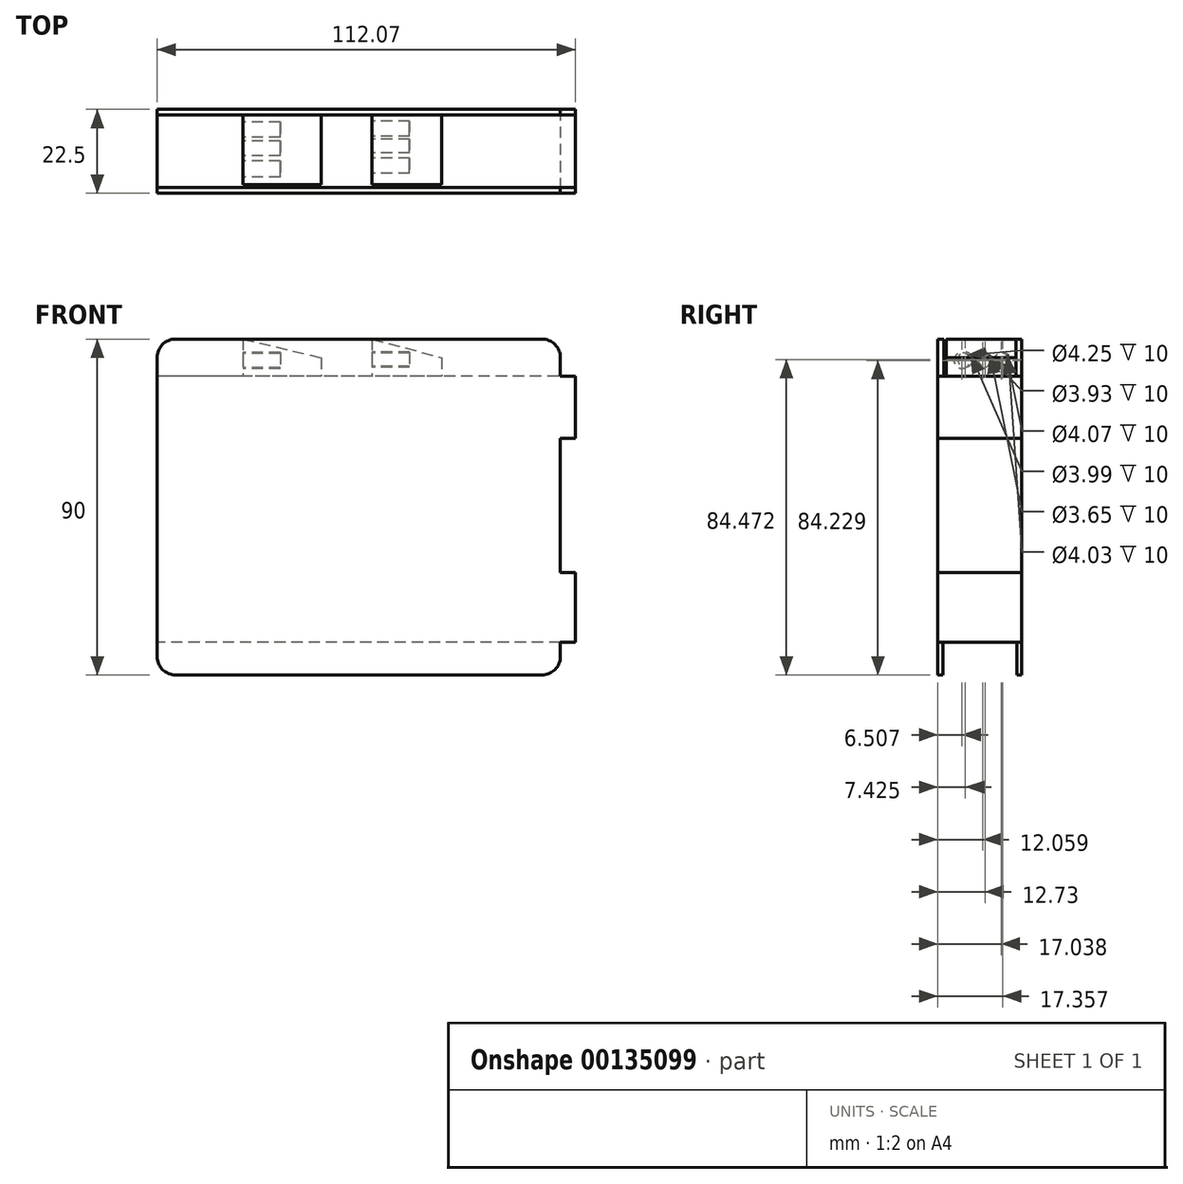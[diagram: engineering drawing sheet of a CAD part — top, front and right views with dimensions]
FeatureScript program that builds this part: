
annotation { "Feature Type Name" : "Feature", "Feature Type Description" : "" }
export const myFeature = defineFeature(function(context is Context, id is Id, definition is map)
    precondition{}
    {
        {
            var Q0;
            Q0=qCreatedBy(makeId("Front.planeOp"),FACE);
            var sketch = newSketch(context, id + "F0", { "sketchPlane" : qUnion([Q0])});
            skLineSegment(sketch, "E0.bottom", {"start": v(-39, -35.05) * mm, "end": v(59, -35.05) * mm});
            skLineSegment(sketch, "E0.top", {"start": v(-39, 54.95) * mm, "end": v(59, 54.95) * mm});
            skLineSegment(sketch, "E0.left", {"start": v(-44, -30.05) * mm, "end": v(-44, 49.95) * mm});
            skLineSegment(sketch, "E0.right", {"start": v(64, -30.05) * mm, "end": v(64, 49.95) * mm});
            skPoint(sketch, "E1.visualSharp", {"position": v(-44, 54.95) * mm});
            skArc(sketch, "E1.filletArc", {"start": v(-39, 54.95) * mm, "mid": v(-42.53, 53.49) * mm, "end": v(-44, 49.95) * mm});
            skPoint(sketch, "E2.visualSharp", {"position": v(64, 54.95) * mm});
            skArc(sketch, "E2.filletArc", {"start": v(64, 49.95) * mm, "mid": v(62.54, 53.49) * mm, "end": v(59, 54.95) * mm});
            skPoint(sketch, "E3.visualSharp", {"position": v(64, -35.05) * mm});
            skArc(sketch, "E3.filletArc", {"start": v(59, -35.05) * mm, "mid": v(62.54, -33.58) * mm, "end": v(64, -30.05) * mm});
            skPoint(sketch, "E4.visualSharp", {"position": v(-44, -35.05) * mm});
            skArc(sketch, "E4.filletArc", {"start": v(-44, -30.05) * mm, "mid": v(-42.53, -33.58) * mm, "end": v(-39, -35.05) * mm});
            skSolve(sketch);
        }
        {
            var Q0;
            Q0=makeQuery(id+"F0.imprint","IMPRINT",FACE,{"disambiguationData":[TD([[makeQuery(id+"F0.imprint","IMPRINT",EDGE,{"derivedFrom":sQuery(id+"F0.wireOp",EDGE,"E0.bottom")}),1.0]])]});
            extrude(context, id + "F1", {"entities" : qUnion([Q0]), "depth" : 22.5 * mm});
        }
        {
            var Q0;
            Q0=makeQuery(id+"F1.opExtrude","SWEPT_FACE",FACE,{"disambiguationData":[OSD([sQuery(id+"F0.wireOp",EDGE,"E0.left")])]});
            var sketch = newSketch(context, id + "F2", { "sketchPlane" : qUnion([Q0])});
            skLineSegment(sketch, "E5.bottom", {"start": v(1.51, 56.28) * mm, "end": v(20.87, 56.28) * mm});
            skLineSegment(sketch, "E5.top", {"start": v(1.51, 44.94) * mm, "end": v(20.87, 44.94) * mm});
            skLineSegment(sketch, "E5.left", {"start": v(1.51, 56.28) * mm, "end": v(1.51, 44.94) * mm});
            skLineSegment(sketch, "E5.right", {"start": v(20.87, 56.28) * mm, "end": v(20.87, 44.94) * mm});
            skLineSegment(sketch, "E6.bottom", {"start": v(1.34, -36.68) * mm, "end": v(21.04, -36.68) * mm});
            skLineSegment(sketch, "E6.top", {"start": v(1.34, -26.21) * mm, "end": v(21.04, -26.21) * mm});
            skLineSegment(sketch, "E6.left", {"start": v(1.34, -36.68) * mm, "end": v(1.34, -26.21) * mm});
            skLineSegment(sketch, "E6.right", {"start": v(21.04, -36.68) * mm, "end": v(21.04, -26.21) * mm});
            skSolve(sketch);
        }
        {
            var Q0;
            {var subQ0=sQuery(id+"F2.wireOp",EDGE,"E5.bottom");Q0=makeQuery(id+"F2.imprint","IMPRINT",FACE,{"disambiguationData":[TD([[makeQuery(id+"F2.imprint","IMPRINT",EDGE,{"derivedFrom":subQ0}),-1.0]])]});}
            var Q1;
            {var subQ0=sQuery(id+"F2.wireOp",EDGE,"E5.top");Q1=makeQuery(id+"F2.imprint","IMPRINT",FACE,{"disambiguationData":[TD([[makeQuery(id+"F2.imprint","IMPRINT",EDGE,{"derivedFrom":subQ0}),1.0]])]});}
            var Q2;
            {var subQ0=sQuery(id+"F2.wireOp",EDGE,"E6.top");Q2=makeQuery(id+"F2.imprint","IMPRINT",FACE,{"disambiguationData":[TD([[makeQuery(id+"F2.imprint","IMPRINT",EDGE,{"derivedFrom":subQ0}),-1.0]])]});}
            var Q3;
            {var subQ0=sQuery(id+"F2.wireOp",EDGE,"E6.bottom");Q3=makeQuery(id+"F2.imprint","IMPRINT",FACE,{"disambiguationData":[TD([[makeQuery(id+"F2.imprint","IMPRINT",EDGE,{"derivedFrom":subQ0}),1.0]])]});}
            extrude(context, id + "F3", {"entities" : qUnion([Q0, Q1, Q2, Q3]), "operationType" : NewBodyOperationType.REMOVE, "oppositeDirection" : true, "depth" : 155.21 * mm});
        }
        {
            var Q0;
            Q0=makeQuery(id+"F3.boolean.opBoolean","COPY",FACE,{"derivedFrom":makeQuery(id+"F3.opExtrude","SWEPT_FACE",FACE,{"disambiguationData":[OSD([sQuery(id+"F2.wireOp",EDGE,"E5.left")])]})});
            var sketch = newSketch(context, id + "F4", { "sketchPlane" : qUnion([Q0])});
            skLineSegment(sketch, "E7.bottom", {"start": v(-21.03, 54.95) * mm, "end": v(0, 54.95) * mm});
            skLineSegment(sketch, "E7.top", {"start": v(-21.03, 44.94) * mm, "end": v(0, 44.94) * mm});
            skLineSegment(sketch, "E7.left", {"start": v(-21.03, 54.95) * mm, "end": v(-21.03, 44.94) * mm});
            skLineSegment(sketch, "E7.right", {"start": v(0, 54.95) * mm, "end": v(0, 44.94) * mm});
            skLineSegment(sketch, "E8.bottom", {"start": v(13.6, 54.95) * mm, "end": v(32.2, 54.95) * mm});
            skLineSegment(sketch, "E8.top", {"start": v(13.6, 44.94) * mm, "end": v(32.2, 44.94) * mm});
            skLineSegment(sketch, "E8.left", {"start": v(13.6, 54.95) * mm, "end": v(13.6, 44.94) * mm});
            skLineSegment(sketch, "E8.right", {"start": v(32.2, 54.95) * mm, "end": v(32.2, 44.94) * mm});
            skLineSegment(sketch, "E9", {"start": v(-21.03, 54.95) * mm, "end": v(0, 49.95) * mm});
            skLineSegment(sketch, "E10", {"start": v(13.6, 54.95) * mm, "end": v(32.2, 49.95) * mm});
            skSolve(sketch);
        }
        {
            var Q0;
            {var subQ0=sQuery(id+"F4.wireOp",EDGE,"E7.top");Q0=makeQuery(id+"F4.imprint","IMPRINT",FACE,{"disambiguationData":[TD([[makeQuery(id+"F4.imprint","IMPRINT",EDGE,{"derivedFrom":subQ0}),-1.0]])]});}
            var Q1;
            {var subQ0=sQuery(id+"F4.wireOp",EDGE,"E8.top");Q1=makeQuery(id+"F4.imprint","IMPRINT",FACE,{"disambiguationData":[TD([[makeQuery(id+"F4.imprint","IMPRINT",EDGE,{"derivedFrom":subQ0}),-1.0]])]});}
            extrude(context, id + "F5", {"entities" : qUnion([Q0, Q1]), "operationType" : NewBodyOperationType.ADD, "depth" : 18.64 * mm});
        }
        {
            var Q0;
            Q0=makeQuery(id+"F5.opExtrude","SWEPT_FACE",FACE,{"disambiguationData":[OSD([sQuery(id+"F4.wireOp",EDGE,"E7.left")])]});
            var sketch = newSketch(context, id + "F6", { "sketchPlane" : qUnion([Q0])});
            skCircle(sketch, "E11", {"center": v(5.46, 49.18) * mm, "radius": 2.03 * mm});
            skCircle(sketch, "E12", {"center": v(10.44, 49.18) * mm, "radius": 1.97 * mm});
            skCircle(sketch, "E13", {"center": v(16, 49.18) * mm, "radius": 2.12 * mm});
            skSolve(sketch);
        }
        {
            var Q0;
            Q0=makeQuery(id+"F6.imprint","IMPRINT",FACE,{"disambiguationData":[TD([[makeQuery(id+"F6.imprint","IMPRINT",EDGE,{"derivedFrom":sQuery(id+"F6.wireOp",EDGE,"E11")}),1.0]])]});
            var Q1;
            Q1=makeQuery(id+"F6.imprint","IMPRINT",FACE,{"disambiguationData":[TD([[makeQuery(id+"F6.imprint","IMPRINT",EDGE,{"derivedFrom":sQuery(id+"F6.wireOp",EDGE,"E12")}),1.0]])]});
            var Q2;
            Q2=makeQuery(id+"F6.imprint","IMPRINT",FACE,{"disambiguationData":[TD([[makeQuery(id+"F6.imprint","IMPRINT",EDGE,{"derivedFrom":sQuery(id+"F6.wireOp",EDGE,"E13")}),1.0]])]});
            var Q3;
            Q3=sQuery(id+"F6.wireOp",EDGE,"E13");
            var Q4;
            Q4=sQuery(id+"F6.wireOp",EDGE,"E12");
            var Q5;
            Q5=sQuery(id+"F6.wireOp",EDGE,"E11");
            extrude(context, id + "F7", {"entities" : qUnion([Q0, Q1, Q2]), "operationType" : NewBodyOperationType.REMOVE, "surfaceEntities" : qUnion([Q3, Q4, Q5]), "oppositeDirection" : true, "depth" : 10 * mm});
        }
        {
            var Q0;
            Q0=makeQuery(id+"F5.opExtrude","SWEPT_FACE",FACE,{"disambiguationData":[OSD([sQuery(id+"F4.wireOp",EDGE,"E8.left")])]});
            var sketch = newSketch(context, id + "F8", { "sketchPlane" : qUnion([Q0])});
            skCircle(sketch, "E14", {"center": v(5.14, 49.42) * mm, "radius": 2.02 * mm});
            skCircle(sketch, "E15", {"center": v(9.77, 49.42) * mm, "radius": 1.82 * mm});
            skCircle(sketch, "E16", {"center": v(15.07, 49.42) * mm, "radius": 2 * mm});
            skSolve(sketch);
        }
        {
            var Q0;
            Q0=makeQuery(id+"F8.imprint","IMPRINT",FACE,{"disambiguationData":[TD([[makeQuery(id+"F8.imprint","IMPRINT",EDGE,{"derivedFrom":sQuery(id+"F8.wireOp",EDGE,"E14")}),1.0]])]});
            var Q1;
            Q1=makeQuery(id+"F8.imprint","IMPRINT",FACE,{"disambiguationData":[TD([[makeQuery(id+"F8.imprint","IMPRINT",EDGE,{"derivedFrom":sQuery(id+"F8.wireOp",EDGE,"E15")}),1.0]])]});
            var Q2;
            Q2=makeQuery(id+"F8.imprint","IMPRINT",FACE,{"disambiguationData":[TD([[makeQuery(id+"F8.imprint","IMPRINT",EDGE,{"derivedFrom":sQuery(id+"F8.wireOp",EDGE,"E16")}),1.0]])]});
            var Q3;
            Q3=sQuery(id+"F8.wireOp",EDGE,"E14");
            var Q4;
            Q4=sQuery(id+"F8.wireOp",EDGE,"E15");
            var Q5;
            Q5=sQuery(id+"F8.wireOp",EDGE,"E16");
            extrude(context, id + "F9", {"entities" : qUnion([Q0, Q1, Q2]), "operationType" : NewBodyOperationType.REMOVE, "surfaceEntities" : qUnion([Q3, Q4, Q5]), "oppositeDirection" : true, "depth" : 10 * mm});
        }
        {
            var Q0;
            Q0=makeQuery(id+"F1.opExtrude","SWEPT_FACE",FACE,{"disambiguationData":[OSD([sQuery(id+"F0.wireOp",EDGE,"E0.right")])]});
            var sketch = newSketch(context, id + "F10", { "sketchPlane" : qUnion([Q0])});
            skLineSegment(sketch, "E17.bottom", {"start": v(-22.5, 44.95) * mm, "end": v(0, 44.95) * mm});
            skLineSegment(sketch, "E17.top", {"start": v(-22.5, 28.36) * mm, "end": v(0, 28.36) * mm});
            skLineSegment(sketch, "E17.left", {"start": v(-22.5, 44.95) * mm, "end": v(-22.5, 28.36) * mm});
            skLineSegment(sketch, "E17.right", {"start": v(0, 44.95) * mm, "end": v(0, 28.36) * mm});
            skLineSegment(sketch, "E18.bottom", {"start": v(-22.5, -26.21) * mm, "end": v(0, -26.21) * mm});
            skLineSegment(sketch, "E18.top", {"start": v(-22.5, -8.56) * mm, "end": v(0, -8.56) * mm});
            skLineSegment(sketch, "E18.left", {"start": v(-22.5, -26.21) * mm, "end": v(-22.5, -8.56) * mm});
            skLineSegment(sketch, "E18.right", {"start": v(0, -26.21) * mm, "end": v(0, -8.56) * mm});
            skSolve(sketch);
        }
        {
            var Q0;
            Q0=makeQuery(id+"F10.imprint","IMPRINT",FACE,{"disambiguationData":[TD([[makeQuery(id+"F10.imprint","IMPRINT",EDGE,{"derivedFrom":sQuery(id+"F10.wireOp",EDGE,"E17.top")}),1.0]])]});
            var Q1;
            Q1=makeQuery(id+"F10.imprint","IMPRINT",FACE,{"disambiguationData":[TD([[makeQuery(id+"F10.imprint","IMPRINT",EDGE,{"derivedFrom":sQuery(id+"F10.wireOp",EDGE,"E18.top")}),-1.0]])]});
            extrude(context, id + "F11", {"entities" : qUnion([Q0, Q1]), "operationType" : NewBodyOperationType.ADD, "depth" : 5.64 * mm});
        }
        {
            var Q0;
            Q0=makeQuery(id+"F11.boolean.opBoolean","MERGE",FACE,{"derivedFrom":[makeQuery(id+"F1.opExtrude","CAP_FACE",FACE,{"disambiguationData":[OSD([sQuery(id+"F0.wireOp",EDGE,"E0.bottom"),sQuery(id+"F0.wireOp",EDGE,"E0.top"),sQuery(id+"F0.wireOp",EDGE,"E0.left"),sQuery(id+"F0.wireOp",EDGE,"E0.right"),sQuery(id+"F0.wireOp",EDGE,"E1.filletArc"),sQuery(id+"F0.wireOp",EDGE,"E2.filletArc"),sQuery(id+"F0.wireOp",EDGE,"E3.filletArc"),sQuery(id+"F0.wireOp",EDGE,"E4.filletArc")])],"isStart":false}),makeQuery(id+"F11.opExtrude","SWEPT_FACE",FACE,{"disambiguationData":[OSD([sQuery(id+"F10.wireOp",EDGE,"E17.left")])]}),makeQuery(id+"F11.opExtrude","SWEPT_FACE",FACE,{"disambiguationData":[OSD([sQuery(id+"F10.wireOp",EDGE,"E18.left")])]})]});
            var sketch = newSketch(context, id + "F12", { "sketchPlane" : qUnion([Q0])});
            skLineSegment(sketch, "E19.bottom", {"start": v(64, 9.9) * mm, "end": v(68, 9.9) * mm});
            skLineSegment(sketch, "E19.top", {"start": v(64, 28.36) * mm, "end": v(68, 28.36) * mm});
            skLineSegment(sketch, "E19.left", {"start": v(64, 9.9) * mm, "end": v(64, 28.36) * mm});
            skLineSegment(sketch, "E19.right", {"start": v(68, 9.9) * mm, "end": v(68, 28.36) * mm});
            skLineSegment(sketch, "E20.top", {"start": v(64, -7.6) * mm, "end": v(68, -7.6) * mm});
            skLineSegment(sketch, "E20.left", {"start": v(64, 9.9) * mm, "end": v(64, -7.6) * mm});
            skLineSegment(sketch, "E20.right", {"start": v(68, 9.9) * mm, "end": v(68, -7.6) * mm});
            skSolve(sketch);
        }
        {
            var Q0;
            Q0=makeQuery(id+"F11.opExtrude","SWEPT_FACE",FACE,{"disambiguationData":[OSD([sQuery(id+"F10.wireOp",EDGE,"E17.top")])]});
            extrude(context, id + "F13", {"entities" : qUnion([Q0]), "operationType" : NewBodyOperationType.ADD, "depth" : 40.33 * mm});
        }
        {
            var Q0;
            Q0=makeQuery(id+"F12.imprint","IMPRINT",FACE,{"disambiguationData":[TD([[makeQuery(id+"F12.imprint","IMPRINT",EDGE,{"derivedFrom":sQuery(id+"F12.wireOp",EDGE,"E19.top")}),1.0]])]});
            var Q1;
            Q1=makeQuery(id+"F12.imprint","IMPRINT",FACE,{"disambiguationData":[TD([[makeQuery(id+"F12.imprint","IMPRINT",EDGE,{"derivedFrom":sQuery(id+"F12.wireOp",EDGE,"E19.bottom")}),-1.0]])]});
            extrude(context, id + "F14", {"entities" : qUnion([Q0, Q1]), "operationType" : NewBodyOperationType.REMOVE, "oppositeDirection" : true, "depth" : 25 * mm});
        }
        {
            var Q0;
            Q0=makeQuery(id+"F14.boolean.opBoolean","COPY",FACE,{"derivedFrom":makeQuery(id+"F14.opExtrude","SWEPT_FACE",FACE,{"disambiguationData":[OSD([sQuery(id+"F12.wireOp",EDGE,"E19.right"),sQuery(id+"F12.wireOp",EDGE,"E20.right")])]})});
            var sketch = newSketch(context, id + "F15", { "sketchPlane" : qUnion([Q0])});
            skLineSegment(sketch, "E21", {"start": v(22.5, -26.14) * mm, "end": v(0, -26.14) * mm});
            skLineSegment(sketch, "E22", {"start": v(0, -26.14) * mm, "end": v(-7.84, 43.54) * mm});
            skLineSegment(sketch, "E23", {"start": v(-7.84, 43.54) * mm, "end": v(21.08, 38.6) * mm});
            skLineSegment(sketch, "E24", {"start": v(21.08, 38.6) * mm, "end": v(22.5, -26.14) * mm});
            skSolve(sketch);
        }
        {
            var Q0;
            Q0=makeQuery(id+"F11.boolean.opBoolean","MERGE",FACE,{"derivedFrom":[makeQuery(id+"F3.boolean.opBoolean","COPY",FACE,{"derivedFrom":makeQuery(id+"F3.opExtrude","SWEPT_FACE",FACE,{"disambiguationData":[OSD([sQuery(id+"F2.wireOp",EDGE,"E6.top")])]})}),makeQuery(id+"F11.opExtrude","SWEPT_FACE",FACE,{"disambiguationData":[OSD([sQuery(id+"F10.wireOp",EDGE,"E18.bottom")])]})]});
            var sketch = newSketch(context, id + "F16", { "sketchPlane" : qUnion([Q0])});
            skLineSegment(sketch, "E25.bottom", {"start": v(68.08, 22.5) * mm, "end": v(69.65, 22.5) * mm});
            skLineSegment(sketch, "E25.top", {"start": v(68.08, 0) * mm, "end": v(69.65, 0) * mm});
            skLineSegment(sketch, "E25.left", {"start": v(68.08, 22.5) * mm, "end": v(68.08, 0) * mm});
            skLineSegment(sketch, "E25.right", {"start": v(69.65, 22.5) * mm, "end": v(69.65, 0) * mm});
            skSolve(sketch);
        }
        {
            var Q0;
            Q0=makeQuery(id+"F16.imprint","IMPRINT",FACE,{"disambiguationData":[TD([[makeQuery(id+"F16.imprint","IMPRINT",EDGE,{"derivedFrom":sQuery(id+"F16.wireOp",EDGE,"E25.bottom")}),1.0]])]});
            extrude(context, id + "F17", {"entities" : qUnion([Q0]), "operationType" : NewBodyOperationType.REMOVE, "oppositeDirection" : true, "depth" : 78.97 * mm});
        }
        {
            var Q0;
            {var subQ0=sQuery(id+"F15.wireOp",EDGE,"E24");var subQ6=sQuery(id+"F12.wireOp",EDGE,"E20.right");var subQ7=makeQuery(id+"F14.boolean.opBoolean","COPY",EDGE,{"derivedFrom":makeQuery(id+"F14.opExtrude","SWEPT_EDGE",EDGE,{"disambiguationData":[OSD([sQuery(id+"F12.wireOp",EDGE,"E20.top"),subQ6])]})});var subQ8=makeQuery(id+"F15.imprint","INTERSECT",VERTEX,{"derivedFrom":[subQ7,subQ0]});Q0=makeQuery(id+"F15.imprint","IMPRINT",FACE,{"disambiguationData":[TD([[makeQuery(id+"F15.imprint","IMPRINT",EDGE,{"disambiguationData":[TD([[subQ8,1.0]])],"derivedFrom":subQ0}),-1.0]])]});}
            extrude(context, id + "F18", {"entities" : qUnion([Q0]), "operationType" : NewBodyOperationType.REMOVE, "oppositeDirection" : true, "depth" : 25 * mm});
        }
        {
            var Q0;
            Q0=makeQuery(id+"F18.boolean.opBoolean","COPY",FACE,{"derivedFrom":makeQuery(id+"F18.opExtrude","SWEPT_FACE",FACE,{"disambiguationData":[OSD([sQuery(id+"F15.wireOp",EDGE,"E24")])]})});
            extrude(context, id + "F19", {"entities" : qUnion([Q0]), "operationType" : NewBodyOperationType.REMOVE, "oppositeDirection" : true, "depth" : 25 * mm});
        }
    });
